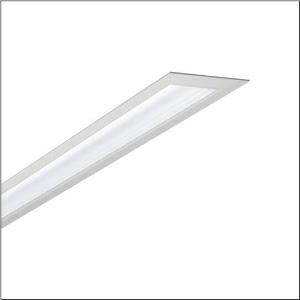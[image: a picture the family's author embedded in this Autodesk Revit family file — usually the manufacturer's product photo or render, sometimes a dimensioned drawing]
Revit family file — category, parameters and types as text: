
# Revit family: silica_r_5mx12wd1w4a_d237
name_source: partatom
category: Lighting Fixtures
units: mm (PartAtom-declared; Revit-internal decimal feet)

## family parameters
Cut with Voids When Loaded = No
Host = Face
Light Source = No
Part Type = Normal
Room Calculation Point = No
Round Connector Dimension = Use Diameter
Shared = No

## types (1)
- --- (1 x LED, 4680 lm, 29.3 W, 4000K)
    Apparent Load = 29 VA
    CIE Flux Codes = 70 95 99 100 100
    Color Rendering = 80
    Color Temperature = 4000K
    Default Elevation = 1800 mm
    Description = Silica®, office luminaire, primary light control with wallwasher, of aluminium, light emission: direct distribution, primary light characteristic: asymmetric, installation type: recessed, LED, rated luminous flux: 4.680lm, luminous efficacy: 160lm/W, light colour: 840, colour temperature: 4000K, control gear: ECG DALI, with terminal, 3+2-pole, max. 2.5mm², mains connection: 230V, AC, 50/60Hz, rated input power: 29W, luminaire housing, of aluminium, matt pure white (RAL 9010), length: 1.462mm, width: 93mm, height: 60mm, end cap, of diecast zinc, pure white (RAL 9010), protection rating (complete): IP20, insulation class (complete): insulation class I (protective earthing), certification: CE, permissible operating ambient temperature: 0..+35°C, standard: EN 50419, packaging unit: 1 piece
    Height = 0 mm  [stored 0 ft]
    Lamp = 1 x LED
    Lamp Light Flux = 4680 lm
    Lamp Power = 29.3 W
    Lamp count = 1
    Length = 1462 mm
    Luminous efficacy = 160 lm/W
    Manufacturer = Siteco
    ModVariant = No
    Model = 5MX12WD1W4A
    Mounting Place = Ceiling
    Mounting Type = Recessed
    Number of Poles = 1
    OnlyDefault = Yes
    Power Factor = 1
    Product Name = Silica®
    Product group = office luminaire | ceiling recessed
    ProductGroupID = 401
    Protection Class = Protection class I
    Protection Degree = IP 20
    RLX_Detail_Level = 1
    RLX_Emergency_Light_Flux = 0 lm
    RLX_Emergency_Type = 0
    RLX_Emergency_Type_DB = No
    RlxData = <blob elided: 24617 chars, md5=c073da62>
    Socket = socket
    Standby Power = 0 W
    System Light Flux = 4680 lm
    System Power = 29 W
    Type Comments = factory setting: luminous flux: 100 % | dim-lin: 254 | 164 mA
    Type Image = l_1004825.jpg
    URL = http://relux.com
    VarID = @adj_138260
    Voltage = 0 V
    Weight = 0.00 kg
    Width = 93 mm

note: [stored X ft] marks values corroborated as IEEE doubles in the binary element streams (Revit-internal decimal feet)

## geometry (parser evidence)
native form markers: Blend x4, Sweep x10
no freeform markers — native parametric forms only
